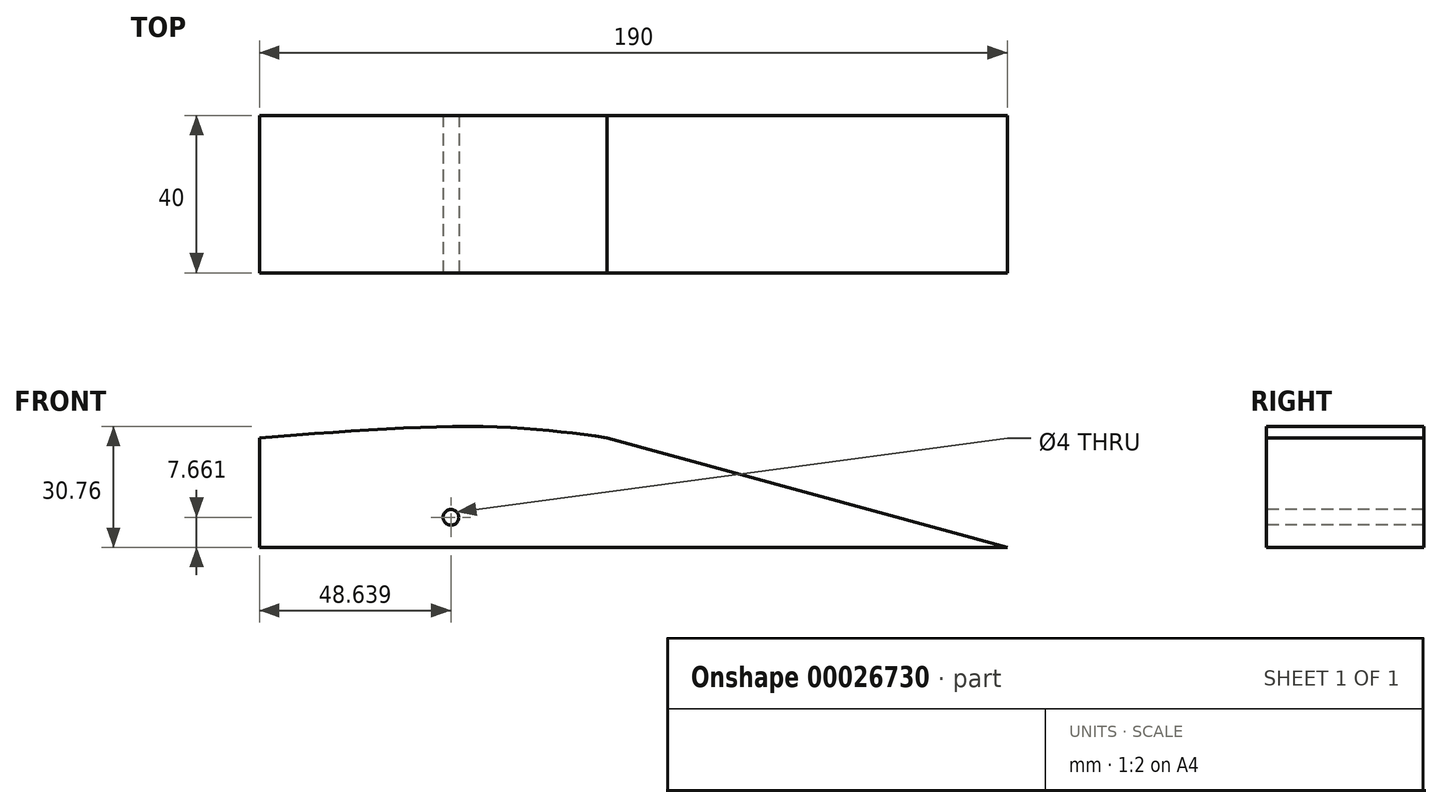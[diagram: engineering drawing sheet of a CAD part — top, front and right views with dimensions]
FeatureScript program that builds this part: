
annotation { "Feature Type Name" : "Feature", "Feature Type Description" : "" }
export const myFeature = defineFeature(function(context is Context, id is Id, definition is map)
    precondition{}
    {
        {
            var Q0;
            Q0=qCreatedBy(makeId("Front.planeOp"),FACE);
            var sketch = newSketch(context, id + "F0", { "sketchPlane" : qUnion([Q0])});
            skLineSegment(sketch, "E0.bottom", {"start": v(-84.2, -32.3) * mm, "end": v(105.8, -32.3) * mm});
            skLineSegment(sketch, "E0.top", {"start": v(-84.2, 37.7) * mm, "end": v(105.8, 37.7) * mm});
            skLineSegment(sketch, "E0.left", {"start": v(-84.2, -32.3) * mm, "end": v(-84.2, 37.7) * mm});
            skLineSegment(sketch, "E0.right", {"start": v(105.8, -32.3) * mm, "end": v(105.8, 37.7) * mm});
            skLineSegment(sketch, "E1", {"start": v(105.8, -32.3) * mm, "end": v(4.05, -4.43) * mm});
            skFitSpline(sketch, "E2", {"points": [v(4.05, -4.43) * mm, v(-26.16, -1.59) * mm, v(-84.2, -4.43) * mm], "startDerivative": vector(-66.16, 9.22) * mm, "endDerivative": vector(-108.1, -8.28) * mm});
            skSolve(sketch);
        }
        {
            var Q0;
            Q0=makeQuery(id+"F0.imprint","IMPRINT",FACE,{"disambiguationData":[TD([[makeQuery(id+"F0.imprint","IMPRINT",EDGE,{"derivedFrom":sQuery(id+"F0.wireOp",EDGE,"E0.bottom")}),1.0]])]});
            extrude(context, id + "F1", {"entities" : qUnion([Q0]), "depth" : 40 * mm});
        }
        {
            var Q0;
            Q0=makeQuery(id+"F1.opExtrude","CAP_FACE",FACE,{"disambiguationData":[OSD([sQuery(id+"F0.wireOp",EDGE,"E0.bottom"),sQuery(id+"F0.wireOp",EDGE,"E0.top"),sQuery(id+"F0.wireOp",EDGE,"E0.left"),sQuery(id+"F0.wireOp",EDGE,"E0.right")])],"isStart":false});
            var sketch = newSketch(context, id + "F2", { "sketchPlane" : qUnion([Q0])});
            skCircle(sketch, "E3", {"center": v(-35.56, -24.64) * mm, "radius": 2 * mm});
            skCircle(sketch, "E4", {"center": v(174.33, -24.64) * mm, "radius": 2 * mm});
            skSolve(sketch);
        }
        {
            var Q0;
            Q0=makeQuery(id+"F2.imprint","IMPRINT",FACE,{"disambiguationData":[TD([[makeQuery(id+"F2.imprint","IMPRINT",EDGE,{"derivedFrom":sQuery(id+"F2.wireOp",EDGE,"E3")}),1.0]])]});
            var Q1;
            Q1=makeQuery(id+"F2.imprint","IMPRINT",FACE,{"disambiguationData":[TD([[makeQuery(id+"F2.imprint","IMPRINT",EDGE,{"derivedFrom":sQuery(id+"F2.wireOp",EDGE,"E4")}),1.0]])]});
            extrude(context, id + "F3", {"entities" : qUnion([Q0, Q1]), "operationType" : NewBodyOperationType.REMOVE, "endBound" : BoundingType.THROUGH_ALL, "oppositeDirection" : true, "depth" : 25 * mm});
        }
    });
